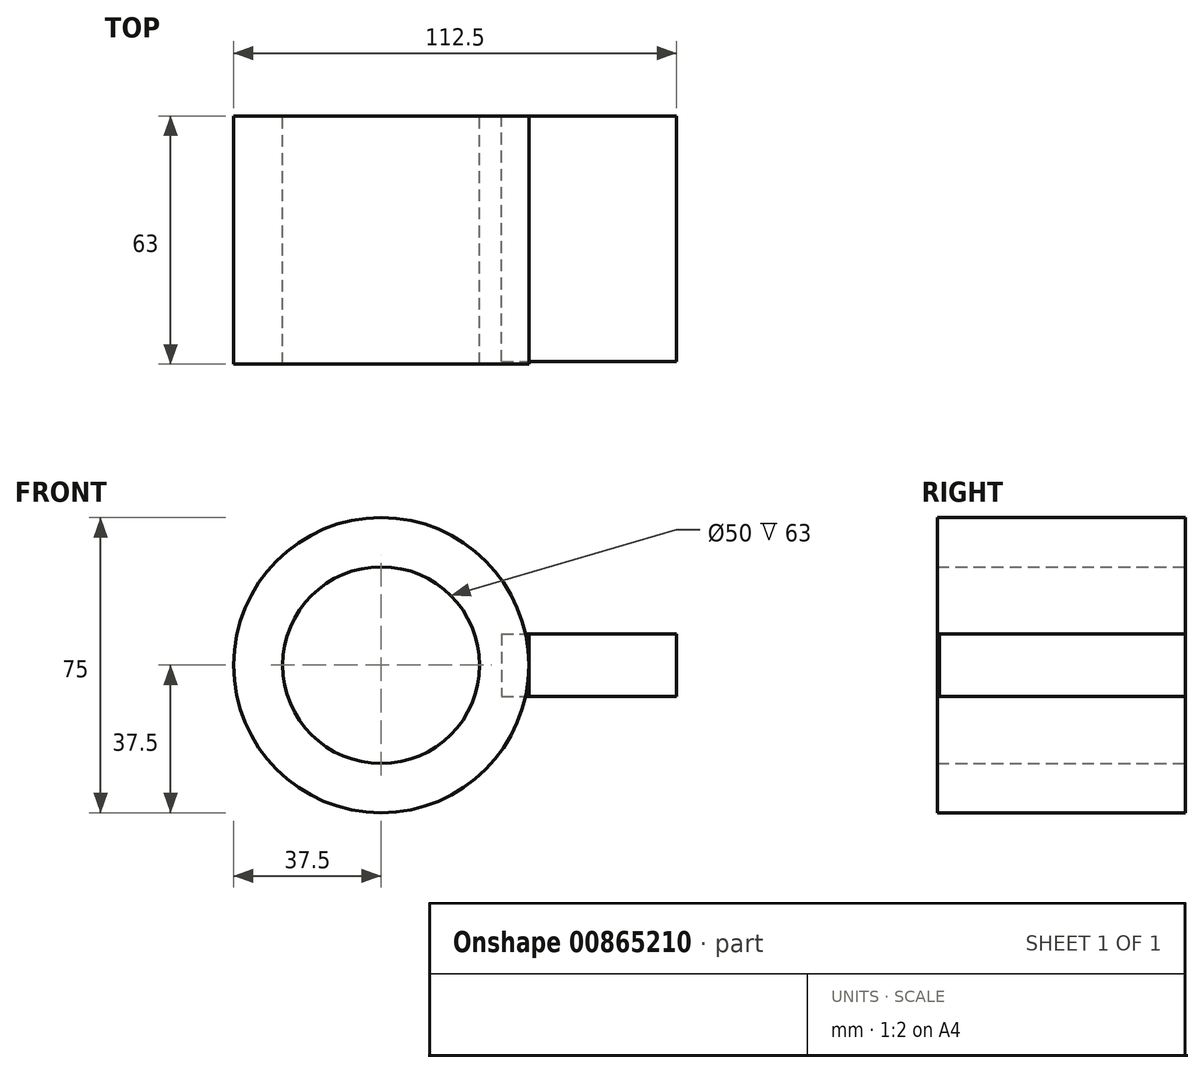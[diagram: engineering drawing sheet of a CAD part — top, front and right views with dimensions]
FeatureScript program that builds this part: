
annotation { "Feature Type Name" : "Feature", "Feature Type Description" : "" }
export const myFeature = defineFeature(function(context is Context, id is Id, definition is map)
    precondition{}
    {
        {
            var Q0;
            Q0=qCreatedBy(makeId("Front.planeOp"),FACE);
            var sketch = newSketch(context, id + "F0", { "sketchPlane" : qUnion([Q0])});
            skCircle(sketch, "E0", {"center": v(0, 0) * mm, "radius": 25 * mm});
            skCircle(sketch, "E1", {"center": v(0, 0) * mm, "radius": 37.5 * mm});
            skSolve(sketch);
        }
        {
            var Q0;
            Q0=makeQuery(id+"F0.imprint","IMPRINT",FACE,{"disambiguationData":[TD([[makeQuery(id+"F0.imprint","IMPRINT",EDGE,{"derivedFrom":sQuery(id+"F0.wireOp",EDGE,"E0")}),-1.0]])]});
            extrude(context, id + "F1", {"entities" : qUnion([Q0]), "depth" : 63 * mm, "offsetDistance" : 25 * mm});
        }
        {
            var Q0;
            Q0=qCreatedBy(makeId("Front.planeOp"),FACE);
            var sketch = newSketch(context, id + "F2", { "sketchPlane" : qUnion([Q0])});
            skLineSegment(sketch, "E2", {"start": v(75, 0) * mm, "end": v(75, 8) * mm});
            skLineSegment(sketch, "E3", {"start": v(75, 0) * mm, "end": v(75, -8) * mm});
            skLineSegment(sketch, "E4", {"start": v(37.5, 8) * mm, "end": v(37.5, -8) * mm});
            skLineSegment(sketch, "E5", {"start": v(75, 8) * mm, "end": v(37.5, 8) * mm});
            skLineSegment(sketch, "E6", {"start": v(75, -8) * mm, "end": v(37.5, -8) * mm});
            skSolve(sketch);
        }
        {
            var Q0;
            Q0=makeQuery(id+"F2.imprint","IMPRINT",FACE,{"disambiguationData":[TD([[makeQuery(id+"F2.imprint","IMPRINT",EDGE,{"derivedFrom":sQuery(id+"F2.wireOp",EDGE,"E2")}),1.0]])]});
            extrude(context, id + "F3", {"entities" : qUnion([Q0]), "operationType" : NewBodyOperationType.ADD, "depth" : 62.4 * mm, "offsetDistance" : 25 * mm});
        }
        {
            var Q0;
            Q0=makeQuery(id+"F3.opExtrude","SWEPT_FACE",FACE,{"disambiguationData":[OSD([sQuery(id+"F2.wireOp",EDGE,"E4")])]});
            extrude(context, id + "F4", {"entities" : qUnion([Q0]), "depth" : 6.9 * mm, "offsetDistance" : 25 * mm});
        }
    });
